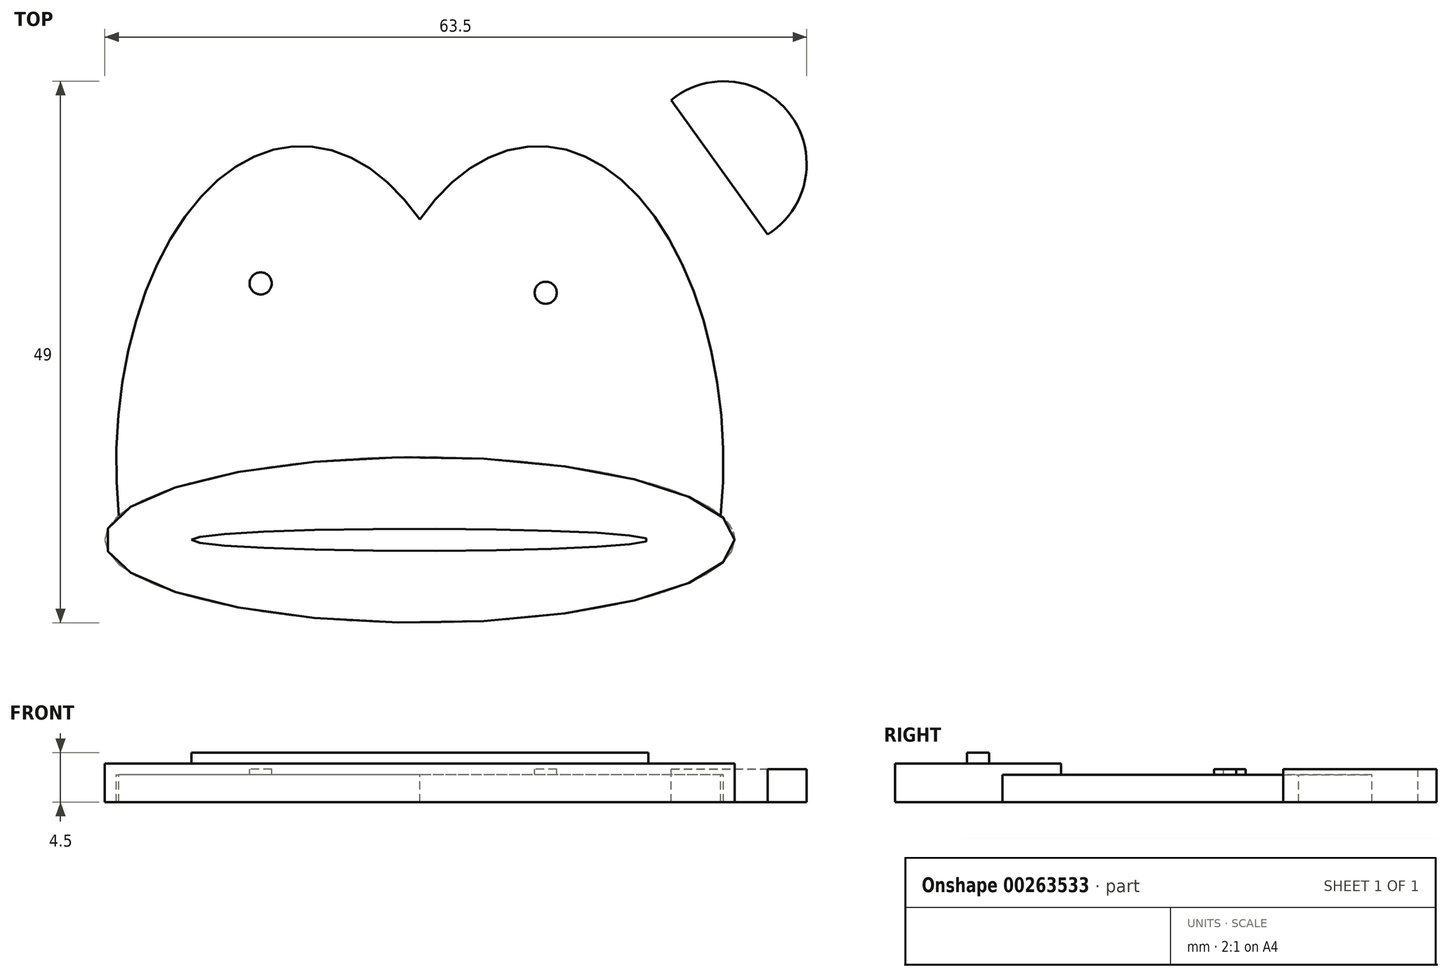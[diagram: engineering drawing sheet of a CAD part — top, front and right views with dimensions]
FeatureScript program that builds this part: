
annotation { "Feature Type Name" : "Feature", "Feature Type Description" : "" }
export const myFeature = defineFeature(function(context is Context, id is Id, definition is map)
    precondition{}
    {
        {
            var Q0;
            Q0=qCreatedBy(makeId("Top.planeOp"),FACE);
            var sketch = newSketch(context, id + "F0", { "sketchPlane" : qUnion([Q0])});
            skArc(sketch, "E0", {"start": v(-32.06, 5.36) * mm, "mid": v(-32, -5.67) * mm, "end": v(-28.27, -16.04) * mm});
            skArc(sketch, "E1", {"start": v(32.06, 5.36) * mm, "mid": v(38.13, 23.57) * mm, "end": v(19.12, 26.28) * mm});
            skArc(sketch, "E2", {"start": v(-19.12, 26.28) * mm, "mid": v(-38.13, 23.57) * mm, "end": v(-32.06, 5.36) * mm});
            skArc(sketch, "E3.trimOffspring", {"start": v(19.12, 26.28) * mm, "mid": v(0, 32.5) * mm, "end": v(-19.12, 26.28) * mm});
            skEllipse(sketch, "E4", {"center": v(0, -17) * mm, "majorRadius": 28.5 * mm, "minorRadius": 7.5 * mm, "majorAxis": v(1, 0)});
            skArc(sketch, "E5.trimOffspring", {"start": v(28.27, -16.04) * mm, "mid": v(32, -5.67) * mm, "end": v(32.06, 5.36) * mm});
            skSolve(sketch);
        }
        {
            var Q0;
            {var subQ0=sQuery(id+"F0.wireOp",EDGE,"E0");Q0=makeQuery(id+"F0.imprint","IMPRINT",FACE,{"disambiguationData":[TD([[makeQuery(id+"F0.imprint","IMPRINT",EDGE,{"derivedFrom":subQ0}),1.0]])]});}
            var Q1;
            {var subQ0=sQuery(id+"F0.wireOp",EDGE,"E4");var subQ1=makeQuery(id+"F0.imprint","INTERSECT",VERTEX,{"derivedFrom":[sQuery(id+"F0.wireOp",EDGE,"E0"),subQ0]});Q1=makeQuery(id+"F0.imprint","IMPRINT",FACE,{"disambiguationData":[TD([[makeQuery(id+"F0.imprint","IMPRINT",EDGE,{"disambiguationData":[TD([[subQ1,1.0]])],"derivedFrom":subQ0}),1.0]])]});}
            extrude(context, id + "F1", {"entities" : qUnion([Q0, Q1]), "depth" : 1 * mm});
        }
        {
            var Q0;
            {var subQ0=sQuery(id+"F0.wireOp",EDGE,"E4");var subQ1=makeQuery(id+"F0.imprint","INTERSECT",VERTEX,{"derivedFrom":[sQuery(id+"F0.wireOp",EDGE,"E0"),subQ0]});Q0=makeQuery(id+"F0.imprint","IMPRINT",FACE,{"disambiguationData":[TD([[makeQuery(id+"F0.imprint","IMPRINT",EDGE,{"disambiguationData":[TD([[subQ1,1.0]])],"derivedFrom":subQ0}),1.0]])]});}
            extrude(context, id + "F2", {"entities" : qUnion([Q0]), "operationType" : NewBodyOperationType.ADD, "depth" : 1.5 * mm});
        }
        {
            var Q0;
            Q0=makeQuery(id+"F1.opExtrude","CAP_FACE",FACE,{"disambiguationData":[OSD([sQuery(id+"F0.wireOp",EDGE,"E0"),sQuery(id+"F0.wireOp",EDGE,"E1"),sQuery(id+"F0.wireOp",EDGE,"E2"),sQuery(id+"F0.wireOp",EDGE,"E3.trimOffspring"),sQuery(id+"F0.wireOp",EDGE,"E4"),sQuery(id+"F0.wireOp",EDGE,"E5.trimOffspring")])],"isStart":false});
            var sketch = newSketch(context, id + "F3", { "sketchPlane" : qUnion([Q0])});
            skEllipticalArc(sketch, "E6", {});
            skCircle(sketch, "E7", {"center": v(-14.4, 6.2) * mm, "radius": 1 * mm});
            skCircle(sketch, "E8", {"center": v(11.39, 5.36) * mm, "radius": 1 * mm});
            skEllipticalArc(sketch, "E9", {});
            skPoint(sketch, "E10", {"position": v(0, 12) * mm});
            skPoint(sketch, "E11", {"position": v(10.71, 18.64) * mm});
            skPoint(sketch, "E12", {"position": v(-6.03, -9.67) * mm});
            skPoint(sketch, "E13", {"position": v(-27.23, -14.79) * mm});
            skPoint(sketch, "E14", {"position": v(27.23, -14.79) * mm});
            skPoint(sketch, "E15", {"position": v(1.56, 9.46) * mm});
            skPoint(sketch, "E16", {"position": v(-16.31, 16.98) * mm});
            skPoint(sketch, "E17.MirrorP", {"position": v(16.31, 16.98) * mm});
            const initialGuessF3  = {"E6": [-0.010712423052355443, -0.010049970643421955, 0, 1, 0.028686105472905246, 0.01674724090429965, 5.589138546215686, 1.7366521922360396], "E9": [0.010712423052355443, -0.010049970643421955, 0, 1, 0.028686105472905246, 0.01674724090429965, 4.546533114943546, 0.694046760963902], "E9": [0.010712423052355443, -0.010049970643421955, 0, 1, 0.028686105472905246, 0.01674724090429965, 4.546533114943546, 0.6940467609639055], "E6": [-0.010712423052355443, -0.010049970643421955, 0, 1, 0.028686105472905246, 0.01674724090429965, 5.589138546215686, 1.7366521922360396], "E9": [0.010712423052355443, -0.010049970643421955, 0, 1, 0.028686105472905246, 0.01674724090429965, 4.546533114943546, 0.694046760963906], "E9": [0.010712423052355443, -0.010049970643421955, 0, 1, 0.028686105472905246, 0.01674724090429965, 4.546533114943546, 0.6940467609639001], "E6": [-0.010712423052355443, -0.010049970643421955, 0, 1, 0.028686105472905246, 0.01674724090429965, 5.589138546215686, 1.7366521922360398]};
            skSetInitialGuess(sketch, initialGuessF3);
            skSolve(sketch);
        }
        {
            var Q0;
            {var subQ1=sQuery(id+"F3.wireOp",EDGE,"E6");Q0=makeQuery(id+"F3.imprint","IMPRINT",FACE,{"disambiguationData":[TD([[makeQuery(id+"F3.imprint","IMPRINT",EDGE,{"derivedFrom":subQ1}),1.0]])]});}
            var Q1;
            Q1=makeQuery(id+"F3.imprint","IMPRINT",FACE,{"disambiguationData":[TD([[makeQuery(id+"F3.imprint","IMPRINT",EDGE,{"derivedFrom":sQuery(id+"F3.wireOp",EDGE,"E7")}),-1.0]])]});
            extrude(context, id + "F4", {"entities" : qUnion([Q0, Q1]), "operationType" : NewBodyOperationType.REMOVE, "oppositeDirection" : true, "depth" : 0.5 * mm});
        }
        {
            var Q0;
            {var subQ0=sQuery(id+"F0.wireOp",EDGE,"E2");var subQ1=sQuery(id+"F0.wireOp",EDGE,"E4");var subQ2=sQuery(id+"F0.wireOp",EDGE,"E5.trimOffspring");var subQ3=sQuery(id+"F0.wireOp",EDGE,"E3.trimOffspring");var subQ4=sQuery(id+"F0.wireOp",EDGE,"E1");var subQ5=sQuery(id+"F0.wireOp",EDGE,"E0");Q0=makeQuery(id+"F4.boolean.opBoolean","SPLIT",FACE,{"disambiguationData":[TD([makeQuery(id+"F1.opExtrude","SWEPT_FACE",FACE,{"disambiguationData":[OSD([subQ5])]})])],"derivedFrom":makeQuery(id+"F1.opExtrude","CAP_FACE",FACE,{"disambiguationData":[OSD([subQ5,subQ4,subQ0,subQ3,subQ1,subQ2])],"isStart":false})});}
            var sketch = newSketch(context, id + "F5", { "sketchPlane" : qUnion([Q0])});
            skArc(sketch, "E18", {"start": v(-23.1, 23.07) * mm, "mid": v(-33.85, 20.98) * mm, "end": v(-31.05, 10.4) * mm});
            skArc(sketch, "E19", {"start": v(22.73, 22.79) * mm, "mid": v(33.6, 21.37) * mm, "end": v(31.46, 10.63) * mm});
            skLineSegment(sketch, "E20", {"start": v(-23.1, 23.07) * mm, "end": v(-31.05, 10.4) * mm});
            skLineSegment(sketch, "E21", {"start": v(22.73, 22.79) * mm, "end": v(31.46, 10.63) * mm});
            skPoint(sketch, "E22.MirrorP", {"position": v(-27.5, -17) * mm});
            skSolve(sketch);
        }
        {
            var Q0;
            Q0=makeQuery(id+"F5.imprint","IMPRINT",FACE,{"disambiguationData":[TD([[makeQuery(id+"F5.imprint","IMPRINT",EDGE,{"derivedFrom":sQuery(id+"F5.wireOp",EDGE,"E18")}),1.0]])]});
            var Q1;
            Q1=makeQuery(id+"F5.imprint","IMPRINT",FACE,{"disambiguationData":[TD([[makeQuery(id+"F5.imprint","IMPRINT",EDGE,{"derivedFrom":sQuery(id+"F5.wireOp",EDGE,"E19")}),-1.0]])]});
            extrude(context, id + "F6", {"entities" : qUnion([Q0, Q1]), "operationType" : NewBodyOperationType.REMOVE, "oppositeDirection" : true, "depth" : 25 * mm});
        }
        {
            var Q0;
            Q0=makeQuery(id+"F2.opExtrude","CAP_FACE",FACE,{"disambiguationData":[OSD([sQuery(id+"F0.wireOp",EDGE,"E4")])],"isStart":false});
            var sketch = newSketch(context, id + "F7", { "sketchPlane" : qUnion([Q0])});
            skEllipse(sketch, "E23", {"center": v(0, -17) * mm, "majorRadius": 20.67 * mm, "minorRadius": 1 * mm, "majorAxis": v(-1, 0)});
            skSolve(sketch);
        }
        {
            var Q0;
            Q0=makeQuery(id+"F7.imprint","IMPRINT",FACE,{"disambiguationData":[TD([[makeQuery(id+"F7.imprint","IMPRINT",EDGE,{"derivedFrom":sQuery(id+"F7.wireOp",EDGE,"E23")}),1.0]])]});
            extrude(context, id + "F8", {"entities" : qUnion([Q0]), "operationType" : NewBodyOperationType.ADD, "depth" : 1 * mm});
        }
        {
            var Q0;
            Q0=makeQuery(id+"F1.opExtrude","CAP_FACE",FACE,{"disambiguationData":[OSD([sQuery(id+"F0.wireOp",EDGE,"E0"),sQuery(id+"F0.wireOp",EDGE,"E1"),sQuery(id+"F0.wireOp",EDGE,"E2"),sQuery(id+"F0.wireOp",EDGE,"E3.trimOffspring"),sQuery(id+"F0.wireOp",EDGE,"E4"),sQuery(id+"F0.wireOp",EDGE,"E5.trimOffspring")])],"isStart":true});
            extrude(context, id + "F9", {"entities" : qUnion([Q0]), "operationType" : NewBodyOperationType.ADD, "depth" : 2 * mm});
        }
    });
